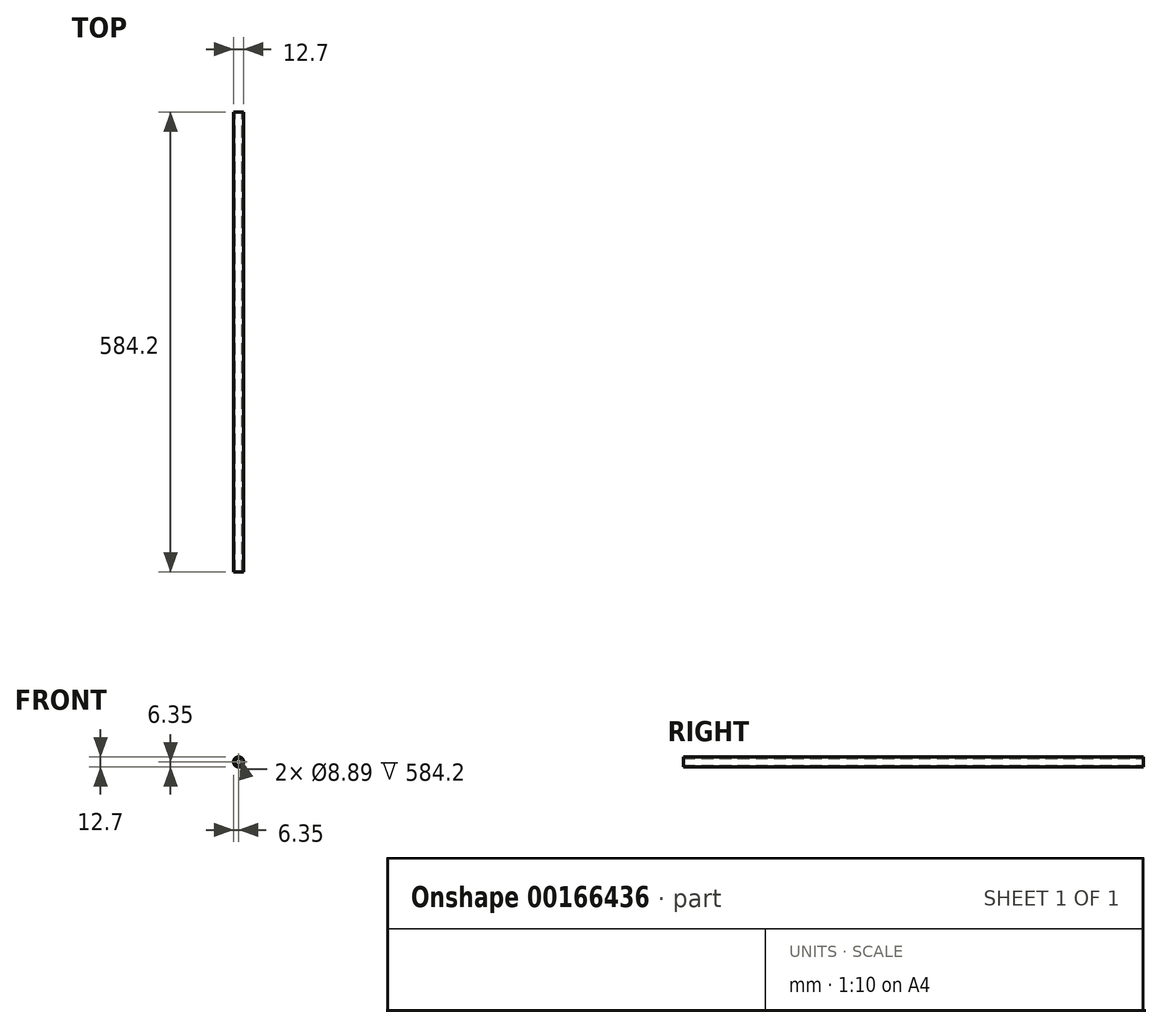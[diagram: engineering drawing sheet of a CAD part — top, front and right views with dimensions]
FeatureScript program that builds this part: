
annotation { "Feature Type Name" : "Feature", "Feature Type Description" : "" }
export const myFeature = defineFeature(function(context is Context, id is Id, definition is map)
    precondition{}
    {
        {
            var Q0;
            Q0=qCreatedBy(makeId("Front.planeOp"),FACE);
            var sketch = newSketch(context, id + "F0", { "sketchPlane" : qUnion([Q0])});
            skCircle(sketch, "E0", {"center": v(0, 0) * mm, "radius": 6.35 * mm});
            skCircle(sketch, "E1", {"center": v(0, 0) * mm, "radius": 4.45 * mm});
            skSolve(sketch);
        }
        {
            var Q0;
            Q0=makeQuery(id+"F0.imprint","IMPRINT",FACE,{"disambiguationData":[TD([[makeQuery(id+"F0.imprint","IMPRINT",EDGE,{"derivedFrom":sQuery(id+"F0.wireOp",EDGE,"E0")}),1.0]])]});
            extrude(context, id + "F1", {"entities" : qUnion([Q0]), "endBound" : BoundingType.SYMMETRIC, "depth" : 584.2 * mm});
        }
    });
